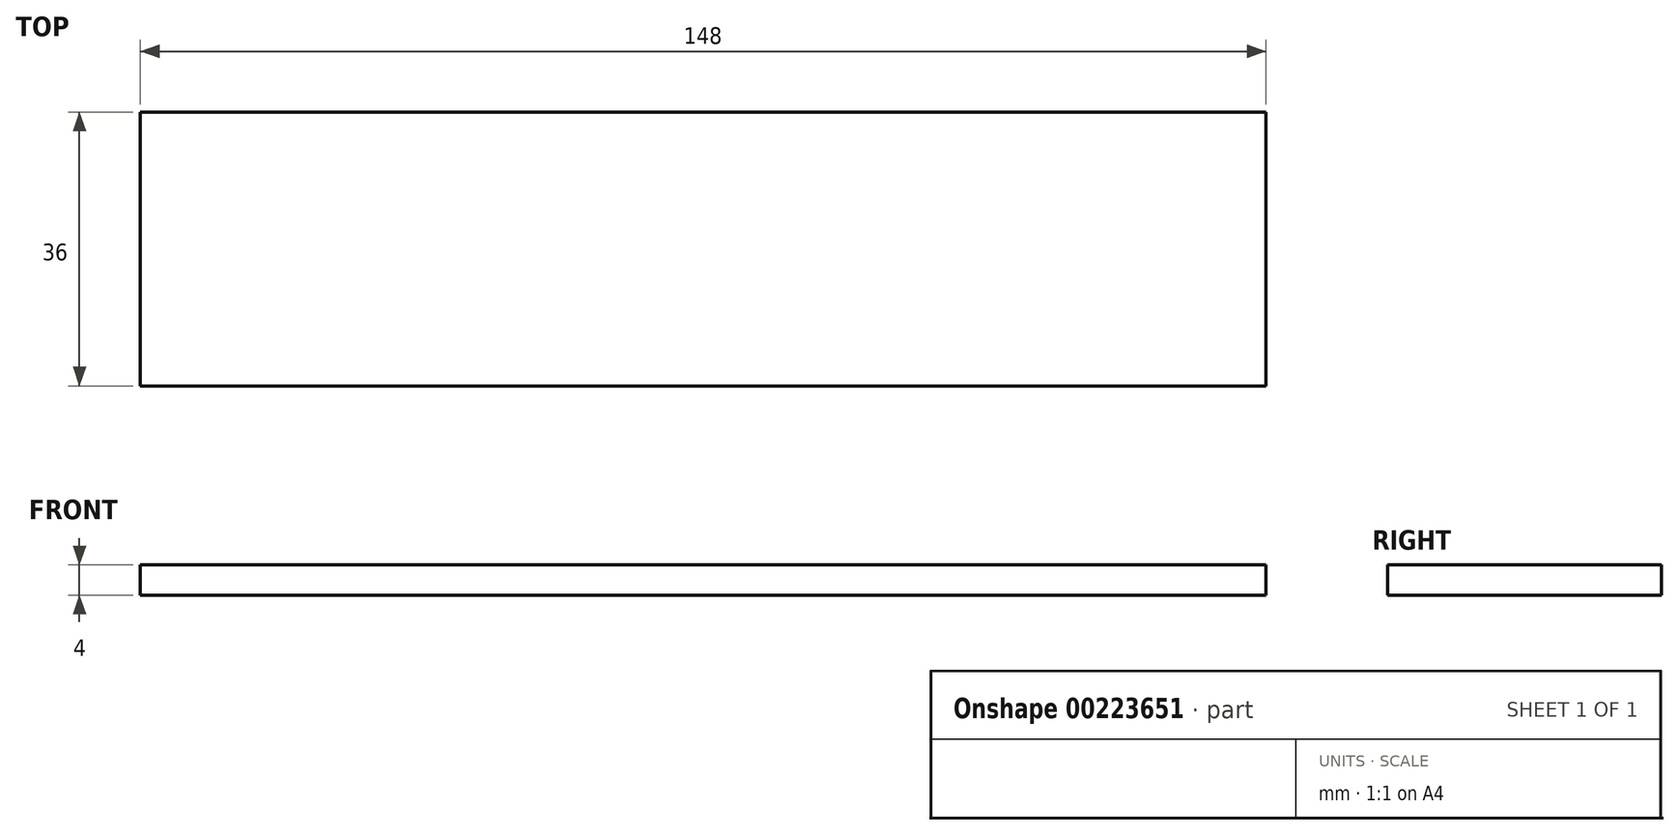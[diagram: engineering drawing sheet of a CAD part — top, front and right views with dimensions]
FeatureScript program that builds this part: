
annotation { "Feature Type Name" : "Feature", "Feature Type Description" : "" }
export const myFeature = defineFeature(function(context is Context, id is Id, definition is map)
    precondition{}
    {
        {
            var Q0;
            Q0=qCreatedBy(makeId("Top.planeOp"),FACE);
            var sketch = newSketch(context, id + "F0", { "sketchPlane" : qUnion([Q0])});
            skLineSegment(sketch, "E0", {"start": v(0, 0) * mm, "end": v(-148, 0) * mm});
            skLineSegment(sketch, "E1", {"start": v(-148, 0) * mm, "end": v(-148, -36) * mm});
            skLineSegment(sketch, "E2", {"start": v(-148, -36) * mm, "end": v(0, -36) * mm});
            skLineSegment(sketch, "E3", {"start": v(0, -36) * mm, "end": v(0, 0) * mm});
            skSolve(sketch);
        }
        {
            var Q0;
            Q0=makeQuery(id+"F0.imprint","IMPRINT",FACE,{"disambiguationData":[TD([[makeQuery(id+"F0.imprint","IMPRINT",EDGE,{"derivedFrom":sQuery(id+"F0.wireOp",EDGE,"E0")}),1.0]])]});
            extrude(context, id + "F1", {"entities" : qUnion([Q0]), "depth" : 4 * mm});
        }
    });
